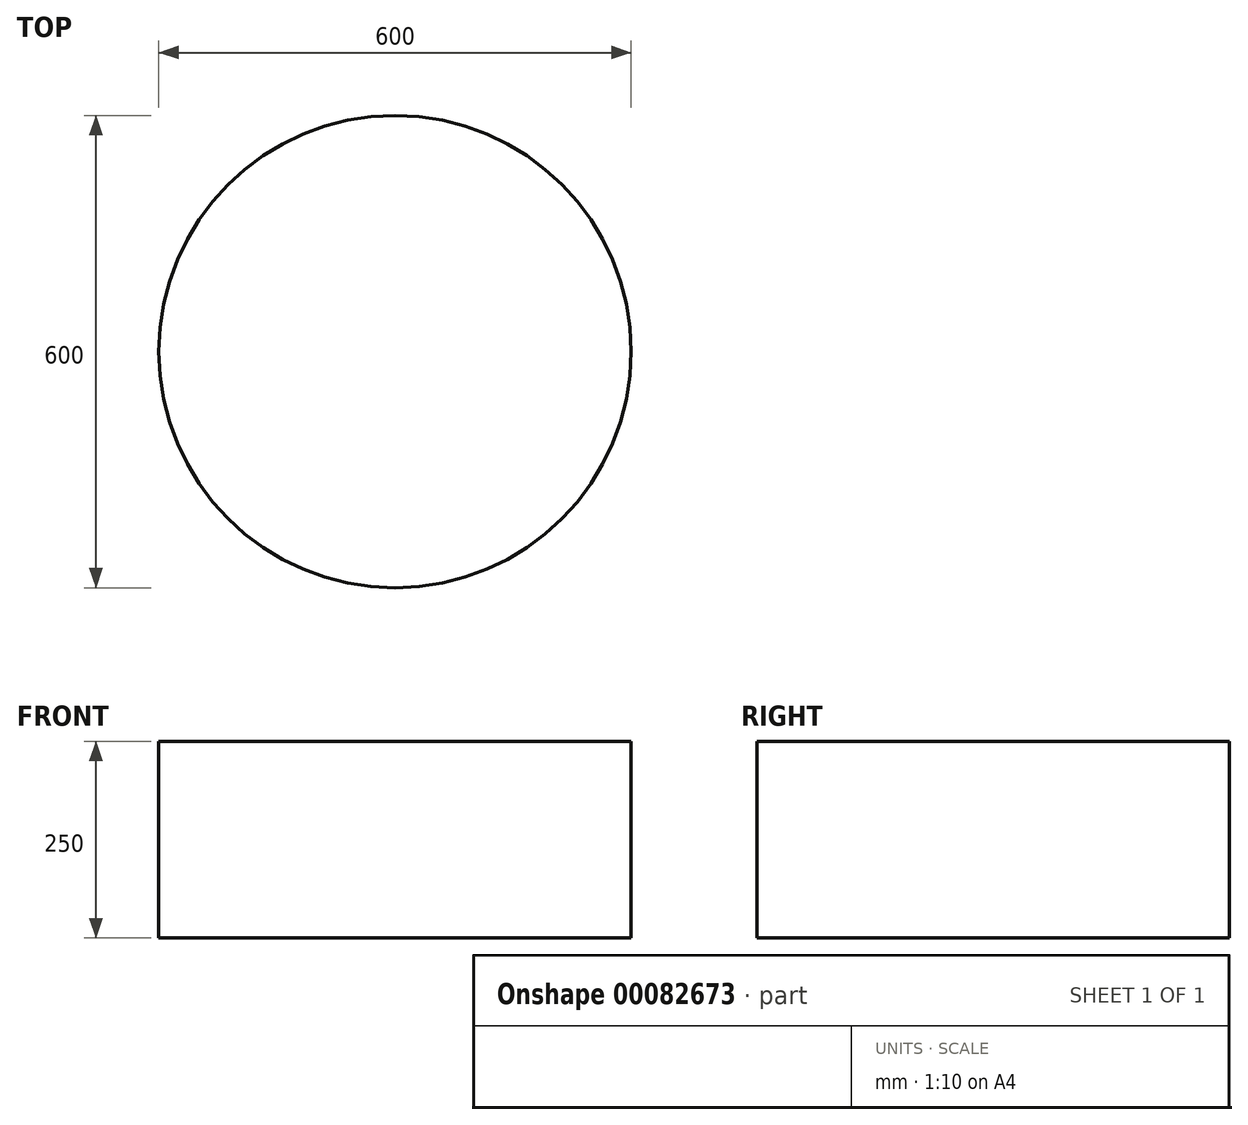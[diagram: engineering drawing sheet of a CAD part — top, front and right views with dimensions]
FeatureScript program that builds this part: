
annotation { "Feature Type Name" : "Feature", "Feature Type Description" : "" }
export const myFeature = defineFeature(function(context is Context, id is Id, definition is map)
    precondition{}
    {
        {
            var Q0;
            Q0=qCreatedBy(makeId("Top.planeOp"),FACE);
            var sketch = newSketch(context, id + "F0", { "sketchPlane" : qUnion([Q0])});
            skCircle(sketch, "E0", {"center": v(0, 0) * mm, "radius": 300 * mm});
            skSolve(sketch);
        }
        {
            var Q0;
            Q0 = qSketchRegion(id + "F0", true);
            extrude(context, id + "F1", {"entities" : qUnion([Q0]), "depth" : 250 * mm});
        }
    });
